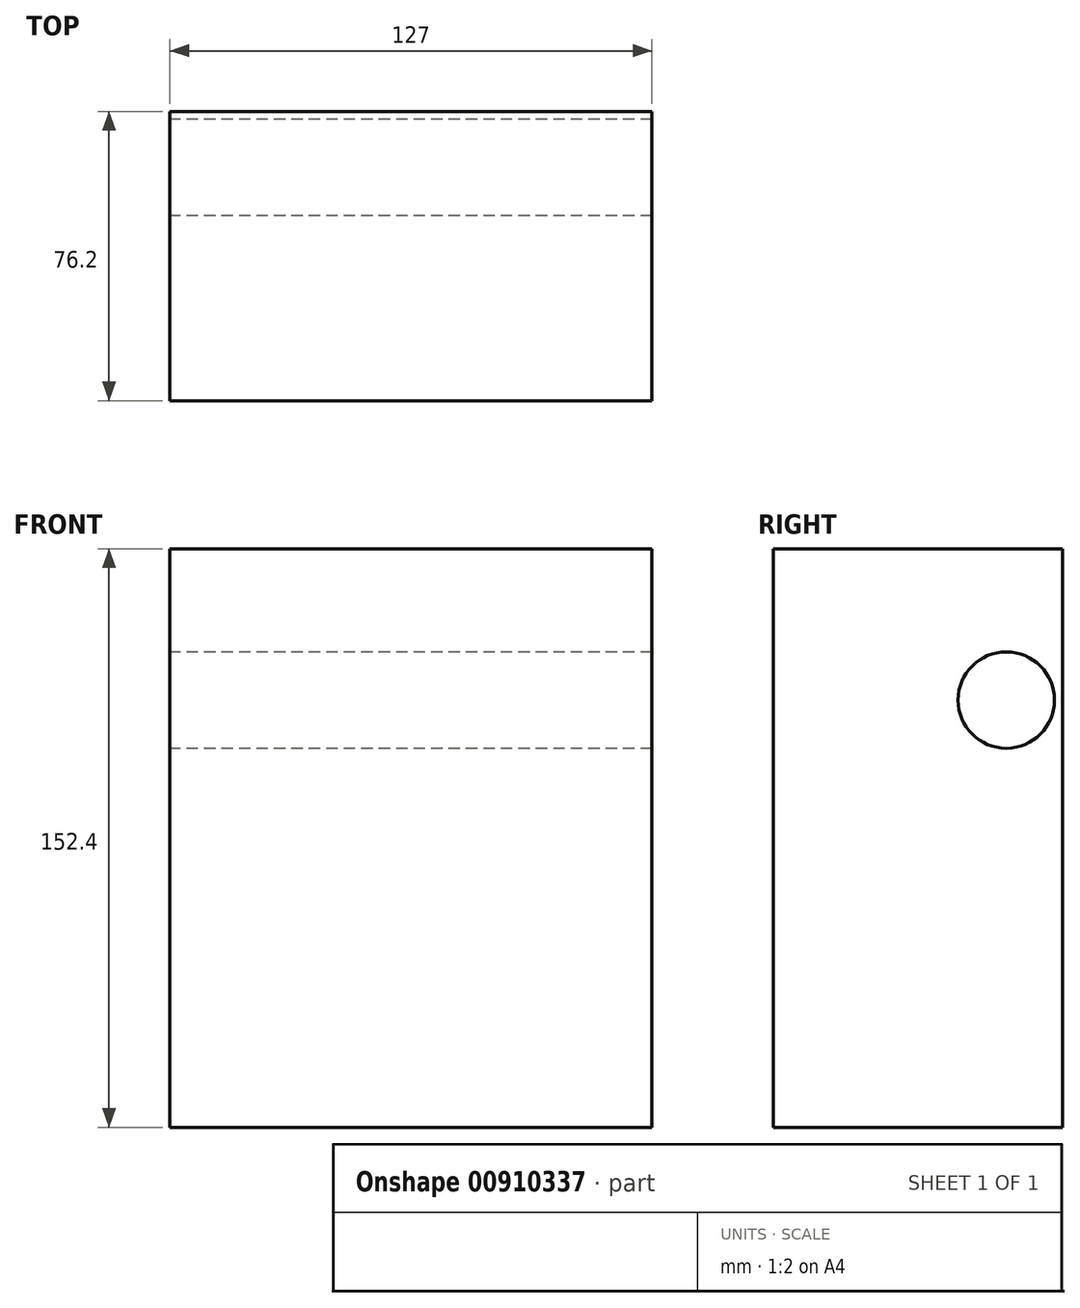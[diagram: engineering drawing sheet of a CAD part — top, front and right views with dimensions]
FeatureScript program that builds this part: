
annotation { "Feature Type Name" : "Feature", "Feature Type Description" : "" }
export const myFeature = defineFeature(function(context is Context, id is Id, definition is map)
    precondition{}
    {
        {
            var Q0;
            Q0=qCreatedBy(makeId("Top.planeOp"),FACE);
            var sketch = newSketch(context, id + "F0", { "sketchPlane" : qUnion([Q0])});
            skLineSegment(sketch, "E0.bottom", {"start": v(0, 9.4) * mm, "end": v(-127, 9.4) * mm});
            skLineSegment(sketch, "E0.top", {"start": v(0, 85.6) * mm, "end": v(-127, 85.6) * mm});
            skLineSegment(sketch, "E0.left", {"start": v(0, 9.4) * mm, "end": v(0, 85.6) * mm});
            skLineSegment(sketch, "E0.right", {"start": v(-127, 9.4) * mm, "end": v(-127, 85.6) * mm});
            skPoint(sketch, "E0.middle", {"position": v(-63.5, 47.5) * mm});
            skSolve(sketch);
        }
        {
            var Q0;
            Q0=makeQuery(id+"F0.imprint","IMPRINT",FACE,{"disambiguationData":[TD([[makeQuery(id+"F0.imprint","IMPRINT",EDGE,{"derivedFrom":sQuery(id+"F0.wireOp",EDGE,"E0.bottom")}),-1.0]])]});
            extrude(context, id + "F1", {"entities" : qUnion([Q0]), "depth" : 152.4 * mm, "offsetDistance" : 25.4 * mm});
        }
        {
            var Q0;
            Q0=makeQuery(id+"F1.opExtrude","SWEPT_FACE",FACE,{"disambiguationData":[OSD([sQuery(id+"F0.wireOp",EDGE,"E0.right")])]});
            var sketch = newSketch(context, id + "F2", { "sketchPlane" : qUnion([Q0])});
            skCircle(sketch, "E1", {"center": v(-70.77, 112.53) * mm, "radius": 12.7 * mm});
            skSolve(sketch);
        }
        {
            var Q0;
            Q0=makeQuery(id+"F2.imprint","IMPRINT",FACE,{"disambiguationData":[TD([[makeQuery(id+"F2.imprint","IMPRINT",EDGE,{"derivedFrom":sQuery(id+"F2.wireOp",EDGE,"E1")}),1.0]])]});
            extrude(context, id + "F3", {"entities" : qUnion([Q0]), "operationType" : NewBodyOperationType.REMOVE, "endBound" : BoundingType.THROUGH_ALL, "oppositeDirection" : true, "depth" : 25.4 * mm, "offsetDistance" : 25.4 * mm});
        }
    });
